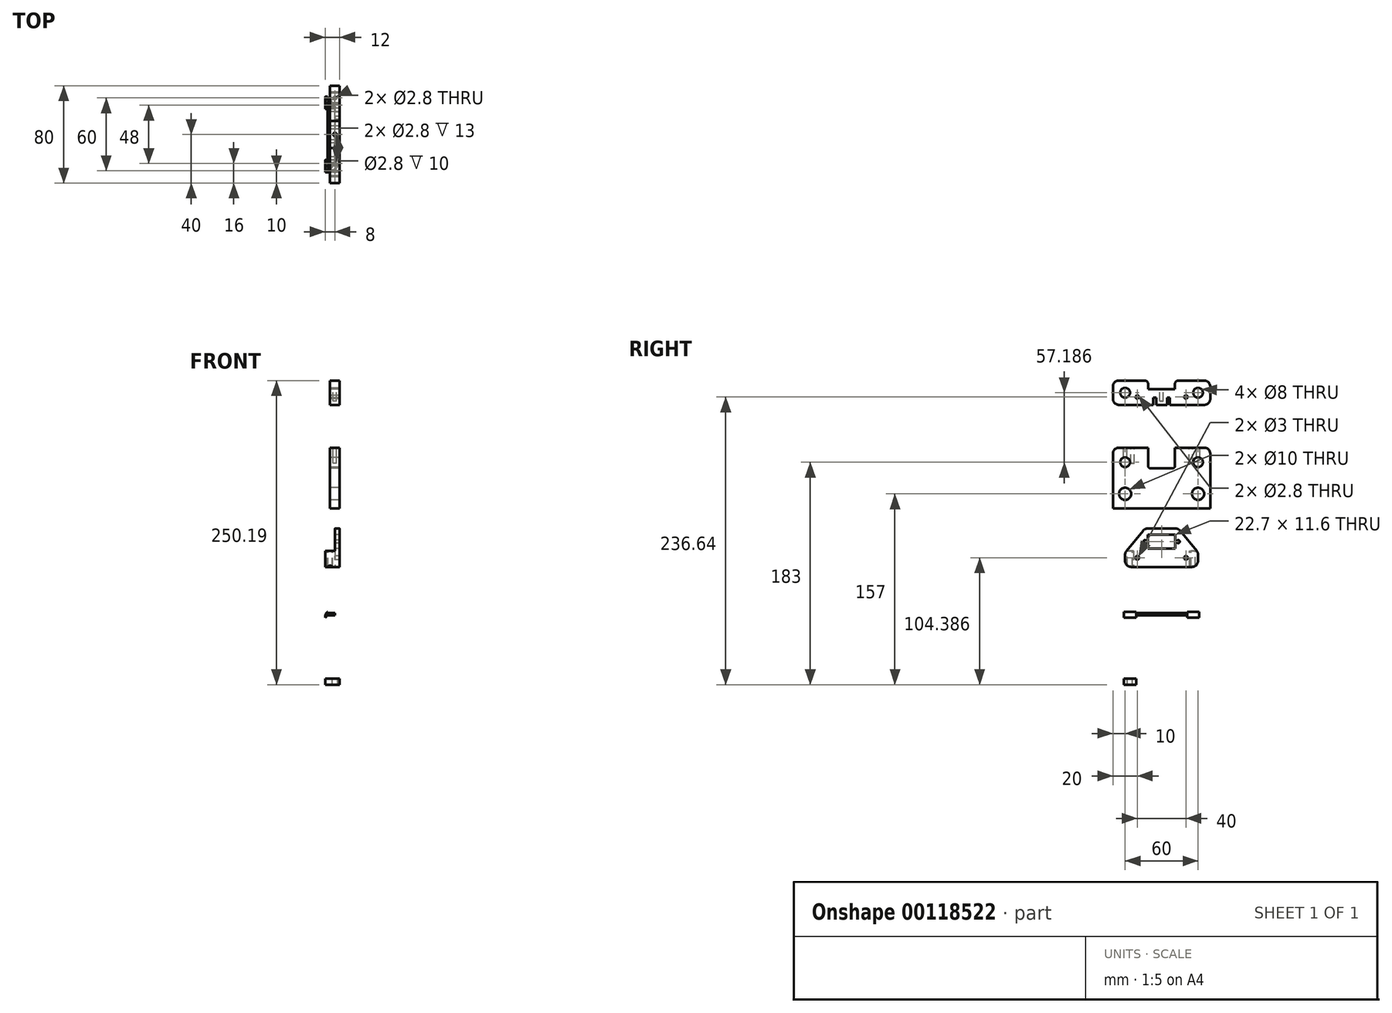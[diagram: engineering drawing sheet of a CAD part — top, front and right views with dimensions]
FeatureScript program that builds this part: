
annotation { "Feature Type Name" : "Feature", "Feature Type Description" : "" }
export const myFeature = defineFeature(function(context is Context, id is Id, definition is map)
    precondition{}
    {
        {
            var Q0;
            Q0=qCreatedBy(makeId("Right.planeOp"),FACE);
            var sketch = newSketch(context, id + "F0", { "sketchPlane" : qUnion([Q0])});
            skLineSegment(sketch, "E0", {"start": v(0, 142.5) * mm, "end": v(0, -139.74) * mm, "construction": true});
            skLineSegment(sketch, "E1.bottom", {"start": v(-35, 25) * mm, "end": v(35, 25) * mm});
            skLineSegment(sketch, "E1.top", {"start": v(-40, -25) * mm, "end": v(40, -25) * mm});
            skLineSegment(sketch, "E1.left", {"start": v(-40, 20) * mm, "end": v(-40, -25) * mm});
            skLineSegment(sketch, "E1.right", {"start": v(40, 20) * mm, "end": v(40, -25) * mm});
            skPoint(sketch, "E1.middle", {"position": v(0, 0) * mm});
            skCircle(sketch, "E2", {"center": v(-30, 13) * mm, "radius": 4 * mm});
            skCircle(sketch, "E3", {"center": v(30, 13) * mm, "radius": 4 * mm});
            skCircle(sketch, "E4", {"center": v(-30, -13) * mm, "radius": 5 * mm});
            skCircle(sketch, "E5", {"center": v(30, -13) * mm, "radius": 5 * mm});
            skPoint(sketch, "E6.visualSharp", {"position": v(-40, 25) * mm});
            skArc(sketch, "E6.filletArc", {"start": v(-35, 25) * mm, "mid": v(-38.54, 23.54) * mm, "end": v(-40, 20) * mm});
            skPoint(sketch, "E7.visualSharp", {"position": v(40, 25) * mm});
            skArc(sketch, "E7.filletArc", {"start": v(40, 20) * mm, "mid": v(38.54, 23.54) * mm, "end": v(35, 25) * mm});
            skLineSegment(sketch, "E8.bottom", {"start": v(-11, 25) * mm, "end": v(11, 25) * mm});
            skLineSegment(sketch, "E8.top", {"start": v(-9, 8) * mm, "end": v(9, 8) * mm});
            skLineSegment(sketch, "E8.left", {"start": v(-11, 25) * mm, "end": v(-11, 10) * mm});
            skLineSegment(sketch, "E8.right", {"start": v(11, 25) * mm, "end": v(11, 10) * mm});
            skPoint(sketch, "E8.middle", {"position": v(0, 16.5) * mm});
            skPoint(sketch, "E9.visualSharp", {"position": v(11, 8) * mm});
            skArc(sketch, "E9.filletArc", {"start": v(9, 8) * mm, "mid": v(10.41, 8.59) * mm, "end": v(11, 10) * mm});
            skPoint(sketch, "E10.visualSharp", {"position": v(-11, 8) * mm});
            skArc(sketch, "E10.filletArc", {"start": v(-11, 10) * mm, "mid": v(-10.41, 8.59) * mm, "end": v(-9, 8) * mm});
            skSolve(sketch);
        }
        {
            var Q0;
            Q0=makeQuery(id+"F0.imprint","IMPRINT",FACE,{"disambiguationData":[TD([[makeQuery(id+"F0.imprint","IMPRINT",EDGE,{"derivedFrom":sQuery(id+"F0.wireOp",EDGE,"E1.bottom")}),-1.0]])]});
            extrude(context, id + "F1", {"entities" : qUnion([Q0]), "depth" : 8 * mm, "symmetric" : true});
        }
        {
            var Q0;
            {var subQ0=sQuery(id+"F0.wireOp",EDGE,"E1.bottom");Q0=makeQuery(id+"F1.opExtrude","SWEPT_FACE",FACE,{"disambiguationData":[OSD([subQ0]),TDD([makeQuery(id+"F0.imprint","IMPRINT",EDGE,{"disambiguationData":[TD([[makeQuery(id+"F0.imprint","INTERSECT",VERTEX,{"derivedFrom":[subQ0,sQuery(id+"F0.wireOp",EDGE,"E7.filletArc")]}),1.0]])],"derivedFrom":subQ0})])]});}
            var sketch = newSketch(context, id + "F2", { "sketchPlane" : qUnion([Q0])});
            skCircle(sketch, "E11", {"center": v(0, 30) * mm, "radius": 1.4 * mm});
            skCircle(sketch, "E12", {"center": v(0, 24) * mm, "radius": 1.4 * mm});
            skCircle(sketch, "E13", {"center": v(0, -24) * mm, "radius": 1.4 * mm});
            skCircle(sketch, "E14", {"center": v(0, -30) * mm, "radius": 1.4 * mm});
            skLineSegment(sketch, "E15", {"start": v(-76.86, 0) * mm, "end": v(82.98, 0) * mm, "construction": true});
            skSolve(sketch);
        }
        {
            var Q0;
            Q0=qSketchRegion(id+"F2",true);
            extrude(context, id + "F3", {"entities" : qUnion([Q0]), "operationType" : NewBodyOperationType.REMOVE, "oppositeDirection" : true, "depth" : 13 * mm});
        }
        {
            var Q0;
            Q0=qCreatedBy(makeId("Right.planeOp"),FACE);
            var sketch = newSketch(context, id + "F4", { "sketchPlane" : qUnion([Q0])});
            skLineSegment(sketch, "E16", {"start": v(0, 90) * mm, "end": v(0, 27.03) * mm, "construction": true});
            skCircle(sketch, "E17", {"center": v(-30, 70.19) * mm, "radius": 4 * mm});
            skCircle(sketch, "E18", {"center": v(30, 70.19) * mm, "radius": 4 * mm});
            skLineSegment(sketch, "E19.bottom", {"start": v(-35, 80.19) * mm, "end": v(35, 80.19) * mm});
            skLineSegment(sketch, "E19.top", {"start": v(-35, 60.19) * mm, "end": v(35, 60.19) * mm});
            skLineSegment(sketch, "E19.left", {"start": v(-40, 75.19) * mm, "end": v(-40, 65.19) * mm});
            skLineSegment(sketch, "E19.right", {"start": v(40, 75.19) * mm, "end": v(40, 65.19) * mm});
            skPoint(sketch, "E19.middle", {"position": v(0, 70.19) * mm});
            skPoint(sketch, "E20.visualSharp", {"position": v(-40, 80.19) * mm});
            skArc(sketch, "E20.filletArc", {"start": v(-35, 80.19) * mm, "mid": v(-38.54, 78.72) * mm, "end": v(-40, 75.19) * mm});
            skPoint(sketch, "E21.visualSharp", {"position": v(-40, 60.19) * mm});
            skArc(sketch, "E21.filletArc", {"start": v(-40, 65.19) * mm, "mid": v(-38.54, 61.65) * mm, "end": v(-35, 60.19) * mm});
            skPoint(sketch, "E22.visualSharp", {"position": v(40, 80.19) * mm});
            skArc(sketch, "E22.filletArc", {"start": v(40, 75.19) * mm, "mid": v(38.54, 78.72) * mm, "end": v(35, 80.19) * mm});
            skPoint(sketch, "E23.visualSharp", {"position": v(40, 60.19) * mm});
            skArc(sketch, "E23.filletArc", {"start": v(35, 60.19) * mm, "mid": v(38.54, 61.65) * mm, "end": v(40, 65.19) * mm});
            skLineSegment(sketch, "E24.bottom", {"start": v(-11, 80.19) * mm, "end": v(11, 80.19) * mm});
            skLineSegment(sketch, "E24.top", {"start": v(-11, 73.19) * mm, "end": v(11, 73.19) * mm});
            skLineSegment(sketch, "E24.left", {"start": v(-11, 80.19) * mm, "end": v(-11, 73.19) * mm});
            skLineSegment(sketch, "E24.right", {"start": v(11, 80.19) * mm, "end": v(11, 73.19) * mm});
            skPoint(sketch, "E24.middle", {"position": v(0, 76.69) * mm});
            skLineSegment(sketch, "E25", {"start": v(-87.97, 70.19) * mm, "end": v(125.2, 70.19) * mm, "construction": true});
            skPoint(sketch, "E25.endSnap0", {"position": v(40, 70.19) * mm});
            skLineSegment(sketch, "E26.bottom", {"start": v(-6.9, 66.19) * mm, "end": v(-4.5, 66.19) * mm});
            skLineSegment(sketch, "E26.top", {"start": v(-6.9, 60.19) * mm, "end": v(-4.5, 60.19) * mm});
            skLineSegment(sketch, "E26.left", {"start": v(-6.9, 66.19) * mm, "end": v(-6.9, 60.19) * mm});
            skLineSegment(sketch, "E26.right", {"start": v(-4.5, 66.19) * mm, "end": v(-4.5, 60.19) * mm});
            skLineSegment(sketch, "E27.bottom", {"start": v(4.5, 66.19) * mm, "end": v(6.9, 66.19) * mm});
            skLineSegment(sketch, "E27.top", {"start": v(4.5, 60.19) * mm, "end": v(6.9, 60.19) * mm});
            skLineSegment(sketch, "E27.left", {"start": v(4.5, 66.19) * mm, "end": v(4.5, 60.19) * mm});
            skLineSegment(sketch, "E27.right", {"start": v(6.9, 66.19) * mm, "end": v(6.9, 60.19) * mm});
            skCircle(sketch, "E28", {"center": v(-20, 66.64) * mm, "radius": 1.4 * mm});
            skCircle(sketch, "E29", {"center": v(20, 66.64) * mm, "radius": 1.4 * mm});
            skSolve(sketch);
        }
        {
            var Q0;
            Q0=makeQuery(id+"F4.imprint","IMPRINT",FACE,{"disambiguationData":[TD([[makeQuery(id+"F4.imprint","IMPRINT",EDGE,{"derivedFrom":sQuery(id+"F4.wireOp",EDGE,"E17")}),-1.0]])]});
            extrude(context, id + "F5", {"entities" : qUnion([Q0]), "depth" : 8 * mm, "symmetric" : true});
        }
        {
            var Q0;
            Q0=makeQuery(id+"F5.opExtrude","SWEPT_EDGE",EDGE,{"disambiguationData":[OSD([sQuery(id+"F4.wireOp",EDGE,"E19.bottom"),sQuery(id+"F4.wireOp",EDGE,"E24.bottom"),sQuery(id+"F4.wireOp",EDGE,"E24.left")])]});
            var Q1;
            Q1=makeQuery(id+"F5.opExtrude","SWEPT_EDGE",EDGE,{"disambiguationData":[OSD([sQuery(id+"F4.wireOp",EDGE,"E19.bottom"),sQuery(id+"F4.wireOp",EDGE,"E24.bottom"),sQuery(id+"F4.wireOp",EDGE,"E24.right")])]});
            fillet(context, id + "F6", {"entities" : qUnion([Q0, Q1]), "radius" : 3 * mm, "tangentPropagation" : true, "allowEdgeOverflow" : false});
        }
        {
            var Q0;
            Q0=makeQuery(id+"F5.opExtrude","SWEPT_FACE",FACE,{"disambiguationData":[OSD([sQuery(id+"F4.wireOp",EDGE,"E24.top")])]});
            var sketch = newSketch(context, id + "F7", { "sketchPlane" : qUnion([Q0])});
            skLineSegment(sketch, "E30", {"start": v(0, 42.64) * mm, "end": v(0, -44.19) * mm, "construction": true});
            skPoint(sketch, "E30.startSnap0", {"position": v(0, 11) * mm});
            skCircle(sketch, "E31", {"center": v(0, 0) * mm, "radius": 1.4 * mm});
            skSolve(sketch);
        }
        {
            var Q0;
            Q0=qSketchRegion(id+"F7",true);
            extrude(context, id + "F8", {"entities" : qUnion([Q0]), "operationType" : NewBodyOperationType.REMOVE, "oppositeDirection" : true, "depth" : 10 * mm});
        }
        {
            var Q0;
            Q0=qCreatedBy(makeId("Right.planeOp"),FACE);
            var sketch = newSketch(context, id + "F9", { "sketchPlane" : qUnion([Q0])});
            skLineSegment(sketch, "E32", {"start": v(-37.85, -65.61) * mm, "end": v(40.06, -65.61) * mm, "construction": true});
            skCircle(sketch, "E33", {"center": v(-20, -65.61) * mm, "radius": 1.5 * mm});
            skCircle(sketch, "E34", {"center": v(20, -65.61) * mm, "radius": 1.5 * mm});
            skLineSegment(sketch, "E35.bottom", {"start": v(-11.35, -58.11) * mm, "end": v(11.35, -58.11) * mm});
            skLineSegment(sketch, "E35.top", {"start": v(-25, -73.11) * mm, "end": v(25, -73.11) * mm});
            skLineSegment(sketch, "E35.left", {"start": v(-30, -63.11) * mm, "end": v(-30, -68.11) * mm});
            skLineSegment(sketch, "E35.right", {"start": v(30, -63.11) * mm, "end": v(30, -68.11) * mm});
            skPoint(sketch, "E35.middle", {"position": v(0, -65.61) * mm});
            skPoint(sketch, "E36.visualSharp", {"position": v(30, -58.11) * mm});
            skArc(sketch, "E36.filletArc", {"start": v(30, -63.11) * mm, "mid": v(29.7, -61.43) * mm, "end": v(28.86, -59.94) * mm});
            skPoint(sketch, "E37.visualSharp", {"position": v(30, -73.11) * mm});
            skArc(sketch, "E37.filletArc", {"start": v(25, -73.11) * mm, "mid": v(28.54, -71.65) * mm, "end": v(30, -68.11) * mm});
            skPoint(sketch, "E38.visualSharp", {"position": v(-30, -73.11) * mm});
            skArc(sketch, "E38.filletArc", {"start": v(-30, -68.11) * mm, "mid": v(-28.54, -71.65) * mm, "end": v(-25, -73.11) * mm});
            skPoint(sketch, "E39.visualSharp", {"position": v(-30, -58.11) * mm});
            skArc(sketch, "E39.filletArc", {"start": v(-28.86, -59.94) * mm, "mid": v(-29.7, -61.43) * mm, "end": v(-30, -63.11) * mm});
            skLineSegment(sketch, "E40.bottom", {"start": v(11.35, -46.51) * mm, "end": v(-11.35, -46.51) * mm});
            skLineSegment(sketch, "E40.top", {"start": v(11.35, -58.11) * mm, "end": v(-11.35, -58.11) * mm});
            skLineSegment(sketch, "E40.left", {"start": v(11.35, -46.51) * mm, "end": v(11.35, -58.11) * mm});
            skLineSegment(sketch, "E40.right", {"start": v(-11.35, -46.51) * mm, "end": v(-11.35, -58.11) * mm});
            skPoint(sketch, "E40.middle", {"position": v(0, -52.31) * mm});
            skPoint(sketch, "E40.middle.positionSnap0", {"position": v(0, -59.61) * mm});
            skArc(sketch, "E41", {"start": v(15.21, -43.34) * mm, "mid": v(13.49, -42) * mm, "end": v(11.35, -41.51) * mm});
            skArc(sketch, "E42", {"start": v(-11.35, -41.51) * mm, "mid": v(-13.49, -42) * mm, "end": v(-15.21, -43.34) * mm});
            skLineSegment(sketch, "E43", {"start": v(15.21, -43.34) * mm, "end": v(30, -61.32) * mm});
            skLineSegment(sketch, "E44", {"start": v(11.35, -41.51) * mm, "end": v(-11.35, -41.51) * mm});
            skLineSegment(sketch, "E45", {"start": v(-15.21, -43.34) * mm, "end": v(-28.86, -59.94) * mm});
            skPoint(sketch, "E46.orphan", {"position": v(25, -58.11) * mm});
            skPoint(sketch, "E47.orphan", {"position": v(-25, -58.11) * mm});
            skLineSegment(sketch, "E48", {"start": v(24.85, -52.31) * mm, "end": v(-24.76, -52.31) * mm, "construction": true});
            skCircle(sketch, "E49", {"center": v(13.67, -52.31) * mm, "radius": 1.25 * mm});
            skCircle(sketch, "E50", {"center": v(-13.67, -52.31) * mm, "radius": 1.25 * mm});
            skSolve(sketch);
        }
        {
            var Q0;
            Q0=qSketchRegion(id+"F9",true);
            extrude(context, id + "F10", {"entities" : qUnion([Q0]), "depth" : 4 * mm});
        }
        {
            var Q0;
            Q0=makeQuery(id+"F10.opExtrude","CAP_FACE",FACE,{"disambiguationData":[OSD([sQuery(id+"F9.wireOp",EDGE,"E33"),sQuery(id+"F9.wireOp",EDGE,"E34"),sQuery(id+"F9.wireOp",EDGE,"E35.top"),sQuery(id+"F9.wireOp",EDGE,"E35.left"),sQuery(id+"F9.wireOp",EDGE,"E35.right"),sQuery(id+"F9.wireOp",EDGE,"E36.filletArc"),sQuery(id+"F9.wireOp",EDGE,"E37.filletArc"),sQuery(id+"F9.wireOp",EDGE,"E38.filletArc"),sQuery(id+"F9.wireOp",EDGE,"E39.filletArc"),sQuery(id+"F9.wireOp",EDGE,"E40.bottom"),sQuery(id+"F9.wireOp",EDGE,"E40.top"),sQuery(id+"F9.wireOp",EDGE,"E40.left"),sQuery(id+"F9.wireOp",EDGE,"E40.right"),sQuery(id+"F9.wireOp",EDGE,"E41"),sQuery(id+"F9.wireOp",EDGE,"E42"),sQuery(id+"F9.wireOp",EDGE,"E43"),sQuery(id+"F9.wireOp",EDGE,"E44"),sQuery(id+"F9.wireOp",EDGE,"E45"),sQuery(id+"F9.wireOp",EDGE,"E49"),sQuery(id+"F9.wireOp",EDGE,"E50")])],"isStart":true});
            var sketch = newSketch(context, id + "F11", { "sketchPlane" : qUnion([Q0])});
            skLineSegment(sketch, "E51.0", {"start": v(-23, -73.11) * mm, "end": v(-23, -59.94) * mm});
            skLineSegment(sketch, "E52", {"start": v(-23, -59.94) * mm, "end": v(-28.86, -59.94) * mm});
            skLineSegment(sketch, "E53", {"start": v(23, -59.94) * mm, "end": v(23, -73.11) * mm});
            skLineSegment(sketch, "E54", {"start": v(23, -59.94) * mm, "end": v(28.86, -59.94) * mm});
            skSolve(sketch);
        }
        {
            var Q0;
            {var subQ2=sQuery(id+"F11.wireOp",EDGE,"E51.0");Q0=makeQuery(id+"F11.imprint","IMPRINT",FACE,{"disambiguationData":[TD([[makeQuery(id+"F11.imprint","IMPRINT",EDGE,{"derivedFrom":subQ2}),1.0]])]});}
            var Q1;
            {var subQ1=sQuery(id+"F11.wireOp",EDGE,"E53");Q1=makeQuery(id+"F11.imprint","IMPRINT",FACE,{"disambiguationData":[TD([[makeQuery(id+"F11.imprint","IMPRINT",EDGE,{"derivedFrom":subQ1}),1.0]])]});}
            extrude(context, id + "F12", {"entities" : qUnion([Q0, Q1]), "operationType" : NewBodyOperationType.ADD, "depth" : 8 * mm});
        }
        {
            var Q0;
            Q0=makeQuery(id+"F12.opExtrude","SWEPT_FACE",FACE,{"disambiguationData":[OSD([sQuery(id+"F11.wireOp",EDGE,"E52")])]});
            var sketch = newSketch(context, id + "F13", { "sketchPlane" : qUnion([Q0])});
            skCircle(sketch, "E55", {"center": v(-4, 25.93) * mm, "radius": 1.72 * mm});
            skPoint(sketch, "E55.centerSnap0", {"position": v(-8, 25.93) * mm});
            skPoint(sketch, "E55.centerSnap1", {"position": v(-4, 23) * mm});
            skCircle(sketch, "E56", {"center": v(-4, -26.07) * mm, "radius": 2 * mm});
            skLineSegment(sketch, "E57", {"start": v(-4, 25.93) * mm, "end": v(-4, -33.93) * mm, "construction": true});
            skSolve(sketch);
        }
        {
            var Q0;
            Q0=qSketchRegion(id+"F13",true);
            extrude(context, id + "F14", {"entities" : qUnion([Q0]), "operationType" : NewBodyOperationType.REMOVE, "oppositeDirection" : true, "depth" : 150 * mm});
        }
        {
            var Q0;
            Q0=makeQuery(id+"F12.opExtrude","CAP_FACE",FACE,{"disambiguationData":[OSD([sQuery(id+"F9.wireOp",EDGE,"E35.top"),sQuery(id+"F9.wireOp",EDGE,"E35.right"),sQuery(id+"F9.wireOp",EDGE,"E36.filletArc"),sQuery(id+"F9.wireOp",EDGE,"E37.filletArc"),sQuery(id+"F11.wireOp",EDGE,"E51.0"),sQuery(id+"F11.wireOp",EDGE,"E52")])],"isStart":false});
            var sketch = newSketch(context, id + "F15", { "sketchPlane" : qUnion([Q0])});
            skLineSegment(sketch, "E58", {"start": v(0, -280) * mm, "end": v(0, 0) * mm, "construction": true});
            skLineSegment(sketch, "E59", {"start": v(-59.5, -140) * mm, "end": v(67.95, -140) * mm, "construction": true});
            skLineSegment(sketch, "E60.bottom", {"start": v(-31, -110) * mm, "end": v(31, -110) * mm});
            skLineSegment(sketch, "E60.top", {"start": v(-31, -170) * mm, "end": v(31, -170) * mm});
            skLineSegment(sketch, "E60.left", {"start": v(-31, -110) * mm, "end": v(-31, -170) * mm});
            skLineSegment(sketch, "E60.right", {"start": v(31, -110) * mm, "end": v(31, -170) * mm});
            skPoint(sketch, "E60.middle", {"position": v(0, -140) * mm});
            skLineSegment(sketch, "E61.bottom", {"start": v(-31, -110) * mm, "end": v(-21, -110) * mm});
            skLineSegment(sketch, "E61.top", {"start": v(-31, -115) * mm, "end": v(-21, -115) * mm});
            skLineSegment(sketch, "E61.left", {"start": v(-31, -110) * mm, "end": v(-31, -115) * mm});
            skLineSegment(sketch, "E61.right", {"start": v(-21, -110) * mm, "end": v(-21, -115) * mm});
            skLineSegment(sketch, "E62.bottom", {"start": v(31, -110) * mm, "end": v(21, -110) * mm});
            skLineSegment(sketch, "E62.top", {"start": v(31, -115) * mm, "end": v(21, -115) * mm});
            skLineSegment(sketch, "E62.left", {"start": v(31, -110) * mm, "end": v(31, -115) * mm});
            skLineSegment(sketch, "E62.right", {"start": v(21, -110) * mm, "end": v(21, -115) * mm});
            skLineSegment(sketch, "E63.bottom", {"start": v(-31, -170) * mm, "end": v(-21, -170) * mm});
            skLineSegment(sketch, "E63.top", {"start": v(-31, -165) * mm, "end": v(-21, -165) * mm});
            skLineSegment(sketch, "E63.left", {"start": v(-31, -170) * mm, "end": v(-31, -165) * mm});
            skLineSegment(sketch, "E63.right", {"start": v(-21, -170) * mm, "end": v(-21, -165) * mm});
            skLineSegment(sketch, "E64.bottom", {"start": v(21, -165) * mm, "end": v(31, -165) * mm});
            skLineSegment(sketch, "E64.top", {"start": v(21, -170) * mm, "end": v(31, -170) * mm});
            skLineSegment(sketch, "E64.left", {"start": v(21, -165) * mm, "end": v(21, -170) * mm});
            skLineSegment(sketch, "E64.right", {"start": v(31, -165) * mm, "end": v(31, -170) * mm});
            skLineSegment(sketch, "E65.bottom", {"start": v(-14.9, -125) * mm, "end": v(-10.9, -125) * mm});
            skLineSegment(sketch, "E65.top", {"start": v(-14.9, -155) * mm, "end": v(-10.9, -155) * mm});
            skLineSegment(sketch, "E65.left", {"start": v(-19.9, -130) * mm, "end": v(-19.9, -150) * mm});
            skLineSegment(sketch, "E65.right", {"start": v(-5.9, -130) * mm, "end": v(-5.9, -150) * mm});
            skLineSegment(sketch, "E66.bottom", {"start": v(10.9, -125) * mm, "end": v(14.9, -125) * mm});
            skLineSegment(sketch, "E66.top", {"start": v(10.9, -155) * mm, "end": v(14.9, -155) * mm});
            skLineSegment(sketch, "E66.left", {"start": v(5.9, -130) * mm, "end": v(5.9, -150) * mm});
            skLineSegment(sketch, "E66.right", {"start": v(19.9, -130) * mm, "end": v(19.9, -150) * mm});
            skPoint(sketch, "E67.visualSharp", {"position": v(-19.9, -125) * mm});
            skArc(sketch, "E67.filletArc", {"start": v(-14.9, -125) * mm, "mid": v(-18.43, -126.46) * mm, "end": v(-19.9, -130) * mm});
            skPoint(sketch, "E68.visualSharp", {"position": v(-5.9, -125) * mm});
            skArc(sketch, "E68.filletArc", {"start": v(-5.9, -130) * mm, "mid": v(-7.36, -126.46) * mm, "end": v(-10.9, -125) * mm});
            skPoint(sketch, "E69.visualSharp", {"position": v(-19.9, -155) * mm});
            skArc(sketch, "E69.filletArc", {"start": v(-19.9, -150) * mm, "mid": v(-18.43, -153.54) * mm, "end": v(-14.9, -155) * mm});
            skPoint(sketch, "E70.visualSharp", {"position": v(-5.9, -155) * mm});
            skArc(sketch, "E70.filletArc", {"start": v(-10.9, -155) * mm, "mid": v(-7.36, -153.54) * mm, "end": v(-5.9, -150) * mm});
            skPoint(sketch, "E71.visualSharp", {"position": v(5.9, -155) * mm});
            skArc(sketch, "E71.filletArc", {"start": v(5.9, -150) * mm, "mid": v(7.36, -153.54) * mm, "end": v(10.9, -155) * mm});
            skPoint(sketch, "E72.visualSharp", {"position": v(5.9, -125) * mm});
            skArc(sketch, "E72.filletArc", {"start": v(10.9, -125) * mm, "mid": v(7.36, -126.46) * mm, "end": v(5.9, -130) * mm});
            skPoint(sketch, "E73.visualSharp", {"position": v(19.9, -155) * mm});
            skArc(sketch, "E73.filletArc", {"start": v(14.9, -155) * mm, "mid": v(18.43, -153.54) * mm, "end": v(19.9, -150) * mm});
            skPoint(sketch, "E74.visualSharp", {"position": v(19.9, -125) * mm});
            skArc(sketch, "E74.filletArc", {"start": v(19.9, -130) * mm, "mid": v(18.43, -126.46) * mm, "end": v(14.9, -125) * mm});
            skCircle(sketch, "E75", {"center": v(0, -125) * mm, "radius": 1.4 * mm});
            skCircle(sketch, "E76", {"center": v(0, -155) * mm, "radius": 1.4 * mm});
            skCircle(sketch, "E77", {"center": v(-22.67, -151.3) * mm, "radius": 1.4 * mm});
            skCircle(sketch, "E78", {"center": v(0, -131.65) * mm, "radius": 1.4 * mm});
            skLineSegment(sketch, "E79", {"start": v(2.62, -129.49) * mm, "end": v(-24.63, -152.98) * mm, "construction": true});
            skSolve(sketch);
        }
        {
            var Q0;
            Q0=makeQuery(id+"F15.imprint","IMPRINT",FACE,{"disambiguationData":[TD([[makeQuery(id+"F15.imprint","IMPRINT",EDGE,{"derivedFrom":sQuery(id+"F15.wireOp",EDGE,"E60.bottom")}),-1.0]])]});
            extrude(context, id + "F16", {"entities" : qUnion([Q0]), "oppositeDirection" : true, "depth" : 2 * mm});
        }
        {
            var Q0;
            Q0=makeQuery(id+"F15.imprint","IMPRINT",FACE,{"disambiguationData":[TD([[makeQuery(id+"F15.imprint","IMPRINT",EDGE,{"derivedFrom":sQuery(id+"F15.wireOp",EDGE,"E61.bottom")}),-1.0]])]});
            var Q1;
            Q1=makeQuery(id+"F15.imprint","IMPRINT",FACE,{"disambiguationData":[TD([[makeQuery(id+"F15.imprint","IMPRINT",EDGE,{"derivedFrom":sQuery(id+"F15.wireOp",EDGE,"E62.bottom")}),1.0]])]});
            var Q2;
            Q2=makeQuery(id+"F15.imprint","IMPRINT",FACE,{"disambiguationData":[TD([[makeQuery(id+"F15.imprint","IMPRINT",EDGE,{"derivedFrom":sQuery(id+"F15.wireOp",EDGE,"E64.bottom")}),-1.0]])]});
            var Q3;
            Q3=makeQuery(id+"F15.imprint","IMPRINT",FACE,{"disambiguationData":[TD([[makeQuery(id+"F15.imprint","IMPRINT",EDGE,{"derivedFrom":sQuery(id+"F15.wireOp",EDGE,"E63.bottom")}),1.0]])]});
            extrude(context, id + "F17", {"entities" : qUnion([Q0, Q1, Q2, Q3]), "operationType" : NewBodyOperationType.ADD, "oppositeDirection" : true, "depth" : 12 * mm});
        }
        {
            var Q0;
            Q0=makeQuery(id+"F17.boolean.opBoolean","MERGE",FACE,{"derivedFrom":[makeQuery(id+"F16.opExtrude","SWEPT_FACE",FACE,{"disambiguationData":[OSD([sQuery(id+"F15.wireOp",EDGE,"E60.bottom")])]}),makeQuery(id+"F17.opExtrude","SWEPT_FACE",FACE,{"disambiguationData":[OSD([sQuery(id+"F15.wireOp",EDGE,"E61.bottom")])]}),makeQuery(id+"F17.opExtrude","SWEPT_FACE",FACE,{"disambiguationData":[OSD([sQuery(id+"F15.wireOp",EDGE,"E62.bottom")])]})]});
            var sketch = newSketch(context, id + "F18", { "sketchPlane" : qUnion([Q0])});
            skLineSegment(sketch, "E80", {"start": v(0, 33.37) * mm, "end": v(0, -30.89) * mm, "construction": true});
            skCircle(sketch, "E81", {"center": v(0, 26) * mm, "radius": 2.1 * mm});
            skPoint(sketch, "E81.centerSnap0", {"position": v(4, 26) * mm});
            skCircle(sketch, "E82", {"center": v(0, -26) * mm, "radius": 2.14 * mm});
            skSolve(sketch);
        }
        {
            var Q0;
            Q0=qSketchRegion(id+"F18",true);
            extrude(context, id + "F19", {"entities" : qUnion([Q0]), "operationType" : NewBodyOperationType.REMOVE, "oppositeDirection" : true, "depth" : 125 * mm});
        }
        {
            var Q0;
            Q0=makeQuery(id+"F16.opExtrude","CAP_EDGE",EDGE,{"disambiguationData":[OSD([sQuery(id+"F15.wireOp",EDGE,"E62.top")])],"isStart":false});
            var Q1;
            Q1=makeQuery(id+"F16.opExtrude","CAP_EDGE",EDGE,{"disambiguationData":[OSD([sQuery(id+"F15.wireOp",EDGE,"E61.top")])],"isStart":false});
            var Q2;
            Q2=makeQuery(id+"F16.opExtrude","CAP_EDGE",EDGE,{"disambiguationData":[OSD([sQuery(id+"F15.wireOp",EDGE,"E64.bottom")])],"isStart":false});
            var Q3;
            Q3=makeQuery(id+"F16.opExtrude","CAP_EDGE",EDGE,{"disambiguationData":[OSD([sQuery(id+"F15.wireOp",EDGE,"E63.top")])],"isStart":false});
            var Q4;
            Q4=makeQuery(id+"F17.boolean.opBoolean","MERGE",EDGE,{"derivedFrom":[makeQuery(id+"F16.opExtrude","CAP_EDGE",EDGE,{"disambiguationData":[OSD([sQuery(id+"F15.wireOp",EDGE,"E60.top")])],"isStart":true}),makeQuery(id+"F17.opExtrude","CAP_EDGE",EDGE,{"disambiguationData":[OSD([sQuery(id+"F15.wireOp",EDGE,"E63.bottom")])],"isStart":true}),makeQuery(id+"F17.opExtrude","CAP_EDGE",EDGE,{"disambiguationData":[OSD([sQuery(id+"F15.wireOp",EDGE,"E64.top")])],"isStart":true})]});
            var Q5;
            Q5=makeQuery(id+"F17.boolean.opBoolean","MERGE",EDGE,{"derivedFrom":[makeQuery(id+"F16.opExtrude","CAP_EDGE",EDGE,{"disambiguationData":[OSD([sQuery(id+"F15.wireOp",EDGE,"E60.bottom")])],"isStart":true}),makeQuery(id+"F17.opExtrude","CAP_EDGE",EDGE,{"disambiguationData":[OSD([sQuery(id+"F15.wireOp",EDGE,"E61.bottom")])],"isStart":true}),makeQuery(id+"F17.opExtrude","CAP_EDGE",EDGE,{"disambiguationData":[OSD([sQuery(id+"F15.wireOp",EDGE,"E62.bottom")])],"isStart":true})]});
            fillet(context, id + "F20", {"entities" : qUnion([Q0, Q1, Q2, Q3, Q4, Q5]), "radius" : 5 * mm, "tangentPropagation" : true, "allowEdgeOverflow" : false});
        }
        {
            var Q0;
            Q0=makeQuery(id+"F17.opExtrude","CAP_EDGE",EDGE,{"disambiguationData":[OSD([sQuery(id+"F15.wireOp",EDGE,"E61.left")])],"isStart":false});
            var Q1;
            Q1=makeQuery(id+"F17.opExtrude","CAP_EDGE",EDGE,{"disambiguationData":[OSD([sQuery(id+"F15.wireOp",EDGE,"E61.right")])],"isStart":false});
            var Q2;
            Q2=makeQuery(id+"F17.opExtrude","CAP_EDGE",EDGE,{"disambiguationData":[OSD([sQuery(id+"F15.wireOp",EDGE,"E62.right")])],"isStart":false});
            var Q3;
            Q3=makeQuery(id+"F17.opExtrude","CAP_EDGE",EDGE,{"disambiguationData":[OSD([sQuery(id+"F15.wireOp",EDGE,"E62.left")])],"isStart":false});
            var Q4;
            Q4=makeQuery(id+"F17.opExtrude","CAP_EDGE",EDGE,{"disambiguationData":[OSD([sQuery(id+"F15.wireOp",EDGE,"E64.left")])],"isStart":false});
            var Q5;
            Q5=makeQuery(id+"F17.opExtrude","CAP_EDGE",EDGE,{"disambiguationData":[OSD([sQuery(id+"F15.wireOp",EDGE,"E64.right")])],"isStart":false});
            var Q6;
            Q6=makeQuery(id+"F17.opExtrude","CAP_EDGE",EDGE,{"disambiguationData":[OSD([sQuery(id+"F15.wireOp",EDGE,"E63.right")])],"isStart":false});
            var Q7;
            Q7=makeQuery(id+"F17.opExtrude","CAP_EDGE",EDGE,{"disambiguationData":[OSD([sQuery(id+"F15.wireOp",EDGE,"E63.left")])],"isStart":false});
            fillet(context, id + "F21", {"entities" : qUnion([Q0, Q1, Q2, Q3, Q4, Q5, Q6, Q7]), "radius" : 5 * mm, "tangentPropagation" : true, "allowEdgeOverflow" : false});
        }
        {
            var Q0;
            Q0=makeQuery(id+"F16.opExtrude","CAP_FACE",FACE,{"disambiguationData":[OSD([sQuery(id+"F15.wireOp",EDGE,"E60.bottom"),sQuery(id+"F15.wireOp",EDGE,"E60.top"),sQuery(id+"F15.wireOp",EDGE,"E60.left"),sQuery(id+"F15.wireOp",EDGE,"E60.right"),sQuery(id+"F15.wireOp",EDGE,"E61.top"),sQuery(id+"F15.wireOp",EDGE,"E61.right"),sQuery(id+"F15.wireOp",EDGE,"E62.top"),sQuery(id+"F15.wireOp",EDGE,"E62.right"),sQuery(id+"F15.wireOp",EDGE,"E63.top"),sQuery(id+"F15.wireOp",EDGE,"E63.right"),sQuery(id+"F15.wireOp",EDGE,"E64.bottom"),sQuery(id+"F15.wireOp",EDGE,"E64.left"),sQuery(id+"F15.wireOp",EDGE,"E65.bottom"),sQuery(id+"F15.wireOp",EDGE,"E65.top"),sQuery(id+"F15.wireOp",EDGE,"E65.left"),sQuery(id+"F15.wireOp",EDGE,"E65.right"),sQuery(id+"F15.wireOp",EDGE,"E66.bottom"),sQuery(id+"F15.wireOp",EDGE,"E66.top"),sQuery(id+"F15.wireOp",EDGE,"E66.left"),sQuery(id+"F15.wireOp",EDGE,"E66.right"),sQuery(id+"F15.wireOp",EDGE,"E67.filletArc"),sQuery(id+"F15.wireOp",EDGE,"E68.filletArc"),sQuery(id+"F15.wireOp",EDGE,"E69.filletArc"),sQuery(id+"F15.wireOp",EDGE,"E70.filletArc"),sQuery(id+"F15.wireOp",EDGE,"E71.filletArc"),sQuery(id+"F15.wireOp",EDGE,"E72.filletArc"),sQuery(id+"F15.wireOp",EDGE,"E73.filletArc"),sQuery(id+"F15.wireOp",EDGE,"E74.filletArc"),sQuery(id+"F15.wireOp",EDGE,"E75"),sQuery(id+"F15.wireOp",EDGE,"E76"),sQuery(id+"F15.wireOp",EDGE,"E77"),sQuery(id+"F15.wireOp",EDGE,"E78")])],"isStart":false});
            var sketch = newSketch(context, id + "F22", { "sketchPlane" : qUnion([Q0])});
            skLineSegment(sketch, "E83.bottom", {"start": v(-21, -111) * mm, "end": v(21, -111) * mm});
            skLineSegment(sketch, "E83.top", {"start": v(-21, -113.02) * mm, "end": v(21, -113.02) * mm});
            skLineSegment(sketch, "E83.left", {"start": v(-21, -111) * mm, "end": v(-21, -113.02) * mm});
            skLineSegment(sketch, "E83.right", {"start": v(21, -111) * mm, "end": v(21, -113.02) * mm});
            skSolve(sketch);
        }
        {
            var Q0;
            Q0=qSketchRegion(id+"F22",true);
            extrude(context, id + "F23", {"entities" : qUnion([Q0]), "operationType" : NewBodyOperationType.ADD, "depth" : 6 * mm});
        }
    });
